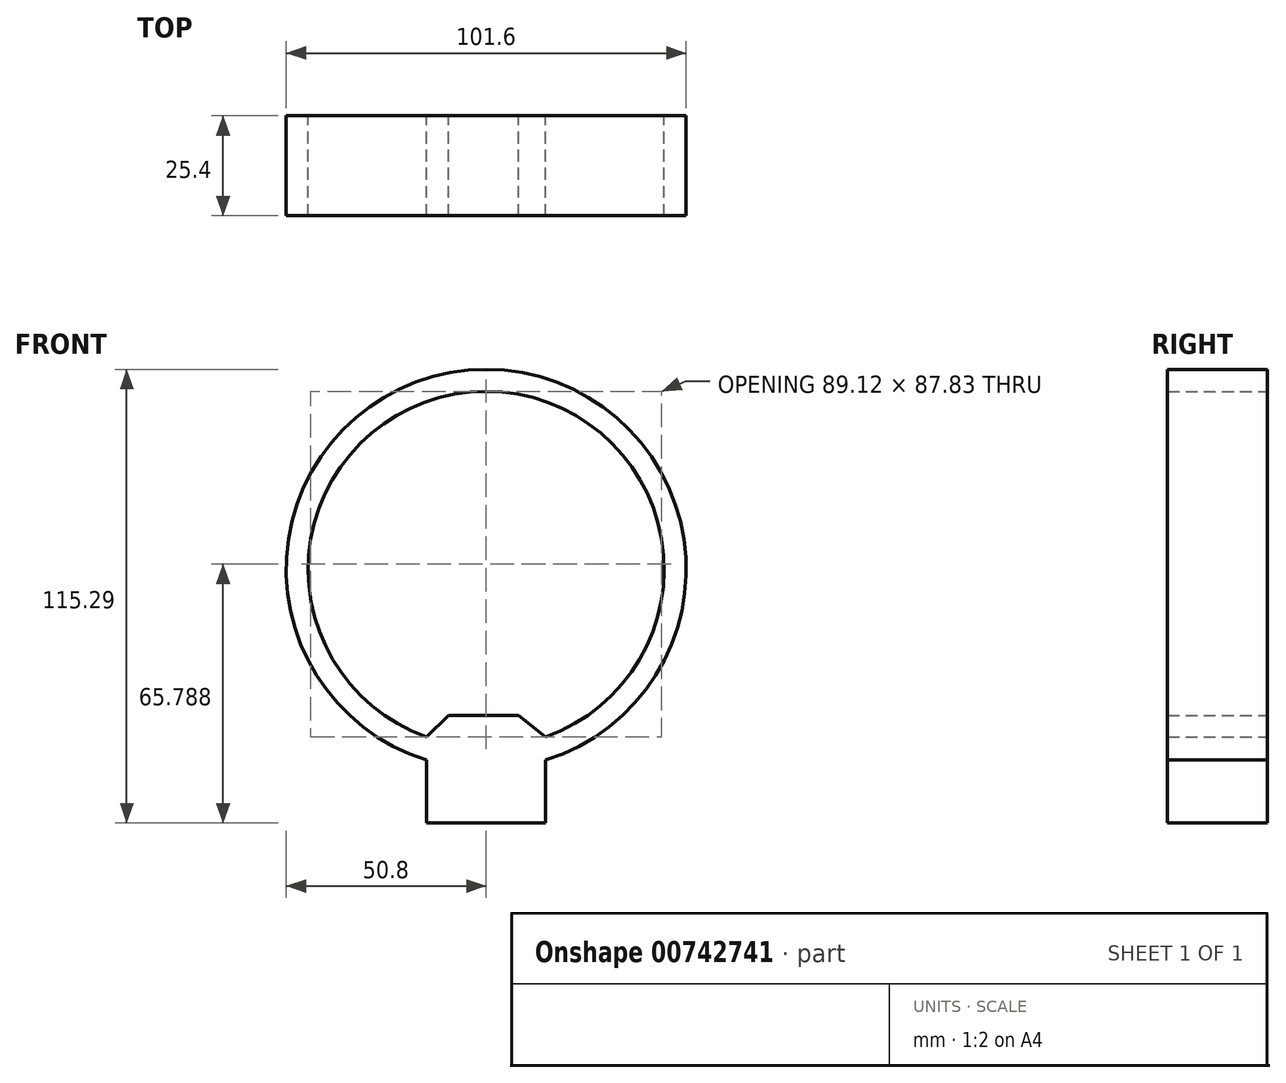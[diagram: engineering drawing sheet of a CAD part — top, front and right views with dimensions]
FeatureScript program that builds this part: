
annotation { "Feature Type Name" : "Feature", "Feature Type Description" : "" }
export const myFeature = defineFeature(function(context is Context, id is Id, definition is map)
    precondition{}
    {
        {
            var Q0;
            Q0=qCreatedBy(makeId("Front.planeOp"),FACE);
            var sketch = newSketch(context, id + "F0", { "sketchPlane" : qUnion([Q0])});
            skArc(sketch, "E0", {"start": v(15.1, -48.5) * mm, "mid": v(0, 50.8) * mm, "end": v(-15.1, -48.5) * mm});
            skArc(sketch, "E1", {"start": v(15.1, -42.62) * mm, "mid": v(0, 45.21) * mm, "end": v(-15.1, -42.62) * mm});
            skLineSegment(sketch, "E2.bottom", {"start": v(15.1, -64.49) * mm, "end": v(-15.1, -64.49) * mm});
            skLineSegment(sketch, "E2.top", {"start": v(8.2, -37.11) * mm, "end": v(-9.5, -37.11) * mm});
            skLineSegment(sketch, "E2.left", {"start": v(15.1, -64.49) * mm, "end": v(15.1, -42.62) * mm});
            skLineSegment(sketch, "E2.right", {"start": v(-15.1, -64.49) * mm, "end": v(-15.1, -42.62) * mm});
            skPoint(sketch, "E2.middle", {"position": v(0, -50.8) * mm});
            skLineSegment(sketch, "E3", {"start": v(-9.5, -37.11) * mm, "end": v(-15.1, -42.62) * mm});
            skLineSegment(sketch, "E4", {"start": v(8.2, -37.11) * mm, "end": v(15.1, -42.62) * mm});
            skPoint(sketch, "E5.orphan", {"position": v(15.1, -37.11) * mm});
            skPoint(sketch, "E6.orphan", {"position": v(-15.1, -37.11) * mm});
            skPoint(sketch, "E7", {"position": v(0, 50.8) * mm});
            skPoint(sketch, "E8", {"position": v(0, -43.69) * mm});
            skPoint(sketch, "E9", {"position": v(0, 45.21) * mm});
            skSolve(sketch);
        }
        {
            var Q0;
            {var subQ0=sQuery(id+"F0.wireOp",EDGE,"E0");Q0=makeQuery(id+"F0.imprint","IMPRINT",FACE,{"disambiguationData":[TD([[makeQuery(id+"F0.imprint","IMPRINT",EDGE,{"derivedFrom":subQ0}),1.0]])]});}
            var Q1;
            {var subQ5=sQuery(id+"F0.wireOp",EDGE,"E2.bottom");Q1=makeQuery(id+"F0.imprint","IMPRINT",FACE,{"disambiguationData":[TD([[makeQuery(id+"F0.imprint","IMPRINT",EDGE,{"derivedFrom":subQ5}),-1.0]])]});}
            extrude(context, id + "F1", {"entities" : qUnion([Q0, Q1]), "depth" : 25.4 * mm, "offsetDistance" : 25.4 * mm});
        }
    });
